# Revit family: 94400407RVM001A
name_source: partatom
category: Equipamentos hidráulicos
revit_build: Autodesk Revit 2016 (Build: 20150220_1215(x64)
units: mm (PartAtom-declared; Revit-internal decimal feet)

## family parameters
Com base no plano de trabalho = Não
Compartilhado = Não
Corte com vazios quando carregados = Não
Cota do conector redondo = Utilizar diâmetro
Ponto de cálculo do ambiente = Não
Sempre na vertical = Sim
Tipo de parte = Normal

## types (1)
- 994400-107 TANQUE DE ENCAIXE 27L
    Comentários de tipos = Ler Manual de Instalação
    Código de montagem = 94400-107 TANQUE DE ENCAIXE 27L
    Descrição = 94400-107 TANQUE DE ENCAIXE 27L
    Desenvolvedor = Factory Cursos & Desenvolvimento
    Diametro = 50  [stored 0.164042 ft]
    Dimensões (mm) = 550 X 450 (dim. total)
    Fabricante = Tramontina
    Modelo = 94400-107 TANQUE DE ENCAIXE 27L
    Site do desenvolvedor = www.factorycursos.com.br
    Tipo de imagem = 94400107_4.jpg
    URL = www.tramontina.com.br

note: [stored X ft] marks values corroborated as IEEE doubles in the binary element streams (Revit-internal decimal feet)
